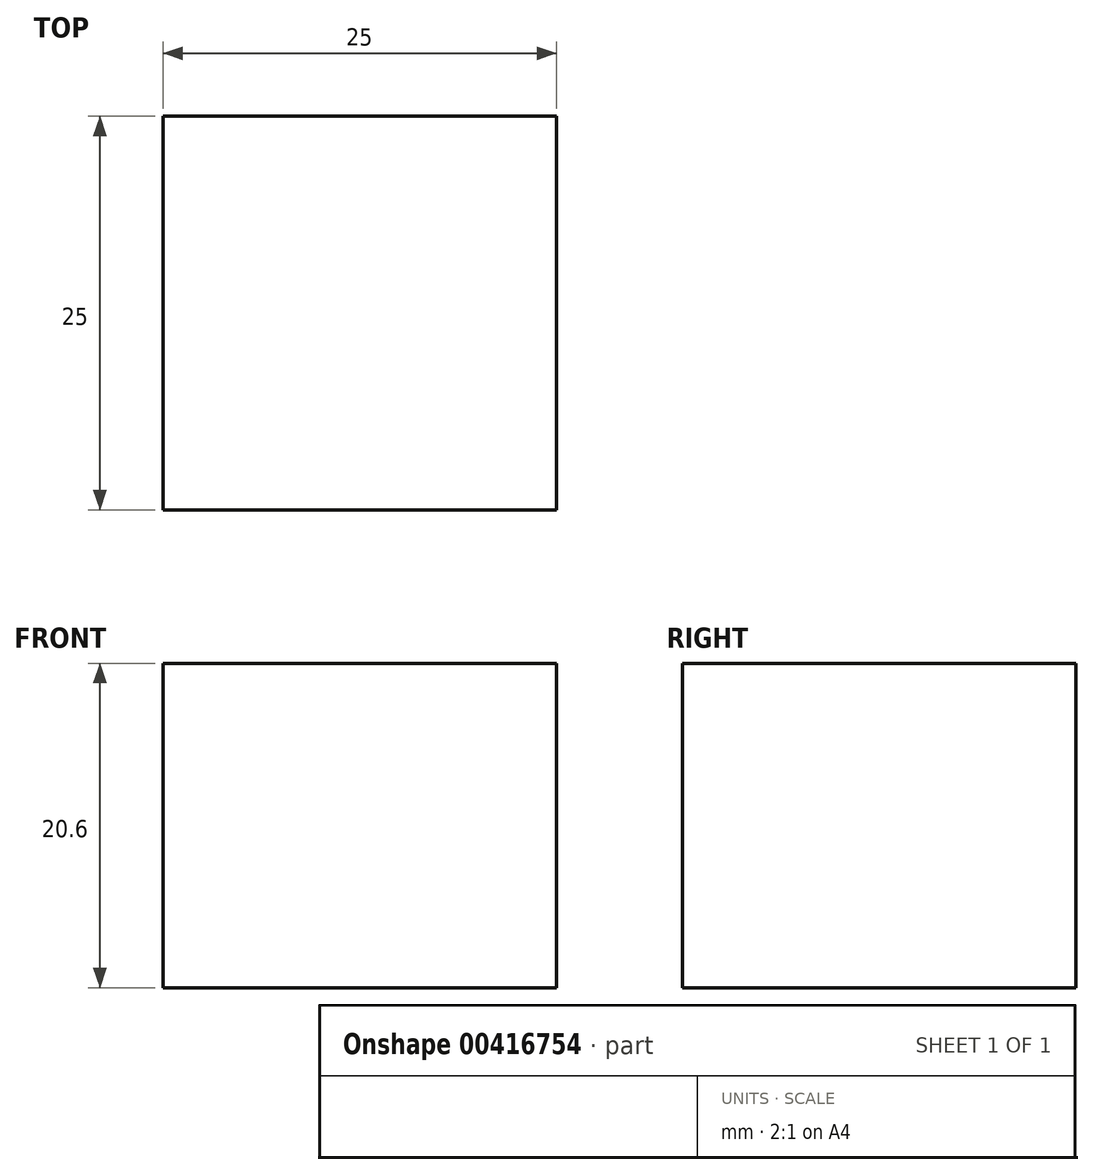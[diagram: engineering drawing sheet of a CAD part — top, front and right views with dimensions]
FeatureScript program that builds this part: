
annotation { "Feature Type Name" : "Feature", "Feature Type Description" : "" }
export const myFeature = defineFeature(function(context is Context, id is Id, definition is map)
    precondition{}
    {
        {
            var Q0;
            Q0=qCreatedBy(makeId("Top.planeOp"),FACE);
            var sketch = newSketch(context, id + "F0", { "sketchPlane" : qUnion([Q0])});
            skLineSegment(sketch, "E0.bottom", {"start": v(0, 0) * mm, "end": v(-25, 0) * mm});
            skLineSegment(sketch, "E0.top", {"start": v(0, 25) * mm, "end": v(-25, 25) * mm});
            skLineSegment(sketch, "E0.left", {"start": v(0, 0) * mm, "end": v(0, 25) * mm});
            skLineSegment(sketch, "E0.right", {"start": v(-25, 0) * mm, "end": v(-25, 25) * mm});
            skSolve(sketch);
        }
        {
            var Q0;
            Q0=makeQuery(id+"F0.imprint","IMPRINT",FACE,{"disambiguationData":[TD([[makeQuery(id+"F0.imprint","IMPRINT",EDGE,{"derivedFrom":sQuery(id+"F0.wireOp",EDGE,"E0.bottom")}),-1.0]])]});
            extrude(context, id + "F1", {"entities" : qUnion([Q0]), "depth" : 20.6 * mm});
        }
    });
